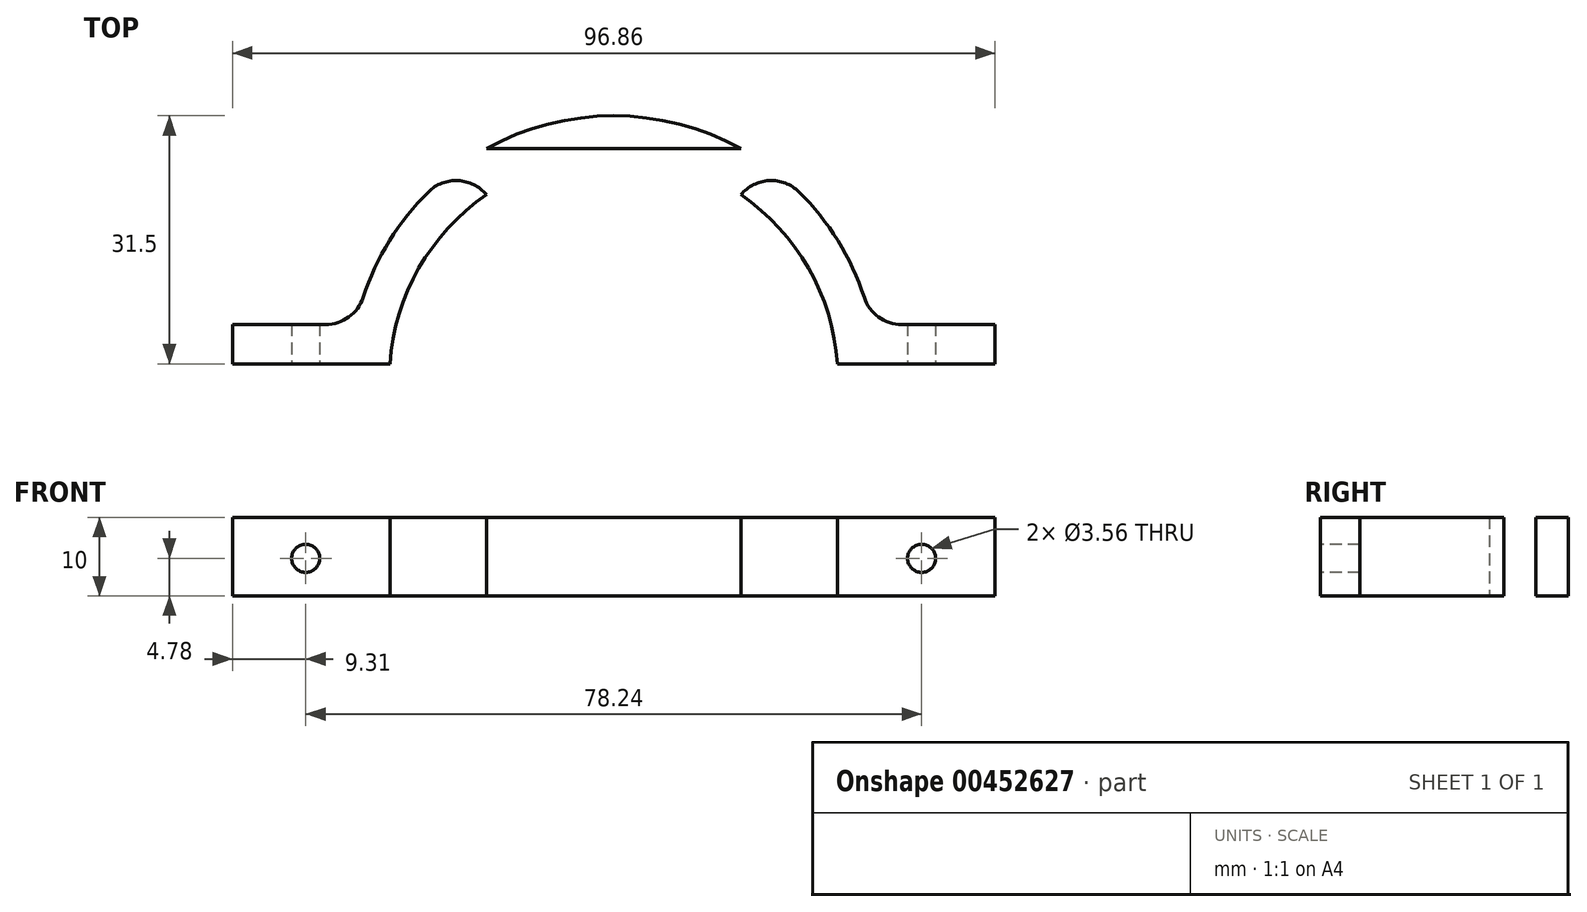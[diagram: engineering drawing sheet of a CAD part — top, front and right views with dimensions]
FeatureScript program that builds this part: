
annotation { "Feature Type Name" : "Feature", "Feature Type Description" : "" }
export const myFeature = defineFeature(function(context is Context, id is Id, definition is map)
    precondition{}
    {
        {
            var Q0;
            Q0=qCreatedBy(makeId("Top.planeOp"),FACE);
            var sketch = newSketch(context, id + "F0", { "sketchPlane" : qUnion([Q0])});
            skCircle(sketch, "E0", {"center": v(0, 0) * mm, "radius": 28.5 * mm, "construction": true});
            skLineSegment(sketch, "E1", {"start": v(-71.53, 0) * mm, "end": v(71.36, 0) * mm, "construction": true});
            skLineSegment(sketch, "E2", {"start": v(-71.7, 2) * mm, "end": v(71.19, 2) * mm, "construction": true});
            skArc(sketch, "E3", {"start": v(28.43, 2) * mm, "mid": v(0, 28.5) * mm, "end": v(-28.43, 2) * mm});
            skArc(sketch, "E4", {"start": v(33.44, 2) * mm, "mid": v(0, 33.5) * mm, "end": v(-33.44, 2) * mm});
            skLineSegment(sketch, "E5", {"start": v(-33.44, 2) * mm, "end": v(-28.43, 2) * mm});
            skLineSegment(sketch, "E6", {"start": v(28.43, 2) * mm, "end": v(33.44, 2) * mm});
            skLineSegment(sketch, "E7.bottom", {"start": v(-28.43, 2) * mm, "end": v(-48.43, 2) * mm});
            skLineSegment(sketch, "E7.top", {"start": v(-28.43, 7) * mm, "end": v(-48.43, 7) * mm});
            skLineSegment(sketch, "E7.left", {"start": v(-28.43, 2) * mm, "end": v(-28.43, 7) * mm});
            skLineSegment(sketch, "E7.right", {"start": v(-48.43, 2) * mm, "end": v(-48.43, 7) * mm});
            skLineSegment(sketch, "E8.bottom", {"start": v(28.43, 2) * mm, "end": v(48.43, 2) * mm});
            skLineSegment(sketch, "E8.top", {"start": v(28.43, 7) * mm, "end": v(48.43, 7) * mm});
            skLineSegment(sketch, "E8.left", {"start": v(28.43, 2) * mm, "end": v(28.43, 7) * mm});
            skLineSegment(sketch, "E8.right", {"start": v(48.43, 2) * mm, "end": v(48.43, 7) * mm});
            skLineSegment(sketch, "E9.bottom", {"start": v(-16.17, 33.5) * mm, "end": v(16.17, 33.5) * mm});
            skLineSegment(sketch, "E9.top", {"start": v(-16.17, 29.34) * mm, "end": v(16.17, 29.34) * mm});
            skLineSegment(sketch, "E9.left", {"start": v(-16.17, 33.5) * mm, "end": v(-16.17, 29.34) * mm});
            skLineSegment(sketch, "E9.right", {"start": v(16.17, 33.5) * mm, "end": v(16.17, 29.34) * mm});
            skPoint(sketch, "E10", {"position": v(0, 33.5) * mm});
            skLineSegment(sketch, "E11.top", {"start": v(-16.17, 23.47) * mm, "end": v(16.17, 23.47) * mm});
            skLineSegment(sketch, "E11.left", {"start": v(-16.17, 29.34) * mm, "end": v(-16.17, 23.47) * mm});
            skLineSegment(sketch, "E11.right", {"start": v(16.17, 29.34) * mm, "end": v(16.17, 23.47) * mm});
            skLineSegment(sketch, "E12.top", {"start": v(-16.17, 38.5) * mm, "end": v(16.17, 38.5) * mm});
            skLineSegment(sketch, "E12.left", {"start": v(-16.17, 33.5) * mm, "end": v(-16.17, 38.5) * mm});
            skLineSegment(sketch, "E12.right", {"start": v(16.17, 33.5) * mm, "end": v(16.17, 38.5) * mm});
            skSolve(sketch);
        }
        {
            var Q0;
            Q0=makeQuery(id+"F0.imprint","IMPRINT",FACE,{"disambiguationData":[TD([[makeQuery(id+"F0.imprint","IMPRINT",EDGE,{"derivedFrom":sQuery(id+"F0.wireOp",EDGE,"E3")}),-1.0]])]});
            var Q1;
            {var subQ5=sQuery(id+"F0.wireOp",EDGE,"E7.right");Q1=makeQuery(id+"F0.imprint","IMPRINT",FACE,{"disambiguationData":[TD([[makeQuery(id+"F0.imprint","IMPRINT",EDGE,{"derivedFrom":subQ5}),-1.0]])]});}
            var Q2;
            {var subQ5=sQuery(id+"F0.wireOp",EDGE,"E7.left");Q2=makeQuery(id+"F0.imprint","IMPRINT",FACE,{"disambiguationData":[TD([[makeQuery(id+"F0.imprint","IMPRINT",EDGE,{"derivedFrom":subQ5}),1.0]])]});}
            var Q3;
            {var subQ5=sQuery(id+"F0.wireOp",EDGE,"E8.left");Q3=makeQuery(id+"F0.imprint","IMPRINT",FACE,{"disambiguationData":[TD([[makeQuery(id+"F0.imprint","IMPRINT",EDGE,{"derivedFrom":subQ5}),-1.0]])]});}
            var Q4;
            {var subQ5=sQuery(id+"F0.wireOp",EDGE,"E8.right");Q4=makeQuery(id+"F0.imprint","IMPRINT",FACE,{"disambiguationData":[TD([[makeQuery(id+"F0.imprint","IMPRINT",EDGE,{"derivedFrom":subQ5}),1.0]])]});}
            var Q5;
            {var subQ0=sQuery(id+"F0.wireOp",EDGE,"E7.left");Q5=makeQuery(id+"F0.imprint","IMPRINT",FACE,{"disambiguationData":[TD([[makeQuery(id+"F0.imprint","IMPRINT",EDGE,{"derivedFrom":subQ0}),-1.0]])]});}
            var Q6;
            {var subQ0=sQuery(id+"F0.wireOp",EDGE,"E9.top");var subQ4=sQuery(id+"F0.wireOp",EDGE,"E3");var subQ7=makeQuery(id+"F0.imprint","INTERSECT",VERTEX,{"disambiguationData":[OD(0.0)],"derivedFrom":[subQ4,subQ0]});Q6=makeQuery(id+"F0.imprint","IMPRINT",FACE,{"disambiguationData":[TD([[makeQuery(id+"F0.imprint","IMPRINT",EDGE,{"disambiguationData":[TD([[subQ7,-1.0]])],"derivedFrom":subQ4}),-1.0]])]});}
            var Q7;
            {var subQ0=sQuery(id+"F0.wireOp",EDGE,"E8.left");Q7=makeQuery(id+"F0.imprint","IMPRINT",FACE,{"disambiguationData":[TD([[makeQuery(id+"F0.imprint","IMPRINT",EDGE,{"derivedFrom":subQ0}),1.0]])]});}
            var Q8;
            {var subQ0=sQuery(id+"F0.wireOp",EDGE,"E9.top");Q8=makeQuery(id+"F0.imprint","IMPRINT",FACE,{"disambiguationData":[TD([[makeQuery(id+"F0.imprint","IMPRINT",EDGE,{"derivedFrom":subQ0}),1.0]])]});}
            extrude(context, id + "F1", {"entities" : qUnion([Q0, Q1, Q2, Q3, Q4, Q5, Q6, Q7, Q8]), "depth" : 10 * mm});
        }
        {
            var Q0;
            Q0=makeQuery(id+"F1.opExtrude","SWEPT_FACE",FACE,{"disambiguationData":[OSD([sQuery(id+"F0.wireOp",EDGE,"E11.top")])]});
            var sketch = newSketch(context, id + "F2", { "sketchPlane" : qUnion([Q0])});
            skPoint(sketch, "E13", {"position": v(0, 5) * mm});
            skLineSegment(sketch, "E14", {"start": v(0, 0) * mm, "end": v(0, 10) * mm, "construction": true});
            skSolve(sketch);
        }
        {
            var Q0;
            Q0=sQuery(id+"F2.wireOp",VERTEX,"E13");
            var Q1;
            Q1=makeQuery(id+"F1.opExtrude","SWEPT_BODY",BODY,{"disambiguationData":[OSD([sQuery(id+"F0.wireOp",EDGE,"E3"),sQuery(id+"F0.wireOp",EDGE,"E4"),sQuery(id+"F0.wireOp",EDGE,"E7.bottom"),sQuery(id+"F0.wireOp",EDGE,"E7.top"),sQuery(id+"F0.wireOp",EDGE,"E7.right"),sQuery(id+"F0.wireOp",EDGE,"E8.bottom"),sQuery(id+"F0.wireOp",EDGE,"E8.top"),sQuery(id+"F0.wireOp",EDGE,"E8.right"),sQuery(id+"F0.wireOp",EDGE,"E9.bottom"),sQuery(id+"F0.wireOp",EDGE,"E9.left"),sQuery(id+"F0.wireOp",EDGE,"E9.right"),sQuery(id+"F0.wireOp",EDGE,"E9.top"),sQuery(id+"F0.wireOp",EDGE,"E11.top")])]});
            hole(context, id + "F3", {"style" : HoleStyle.C_BORE, "endStyle" : HoleEndStyle.THROUGH, "holeDiameter" : 3.56 * mm, "cBoreDiameter" : 7.62 * mm, "cBoreDepth" : 10 * mm, "isTappedThrough" : true, "tappedDepth" : 12 * mm, "tapClearance" : 3, "locations" : qUnion([Q0]), "scope" : qUnion([Q1])});
        }
        {
            var Q0;
            {var subQ0=sQuery(id+"F0.wireOp",EDGE,"E11.top");Q0=makeQuery(id+"F0.imprint","IMPRINT",FACE,{"disambiguationData":[TD([[makeQuery(id+"F0.imprint","IMPRINT",EDGE,{"derivedFrom":subQ0}),1.0]])]});}
            extrude(context, id + "F4", {"entities" : qUnion([Q0]), "operationType" : NewBodyOperationType.REMOVE, "endBound" : BoundingType.THROUGH_ALL, "depth" : 25 * mm});
        }
        {
            var Q0;
            Q0=makeQuery(id+"F1.opExtrude","SWEPT_FACE",FACE,{"disambiguationData":[OSD([sQuery(id+"F0.wireOp",EDGE,"E7.bottom")])]});
            var sketch = newSketch(context, id + "F5", { "sketchPlane" : qUnion([Q0])});
            skPoint(sketch, "E15", {"position": v(-39.12, 4.78) * mm});
            skPoint(sketch, "E16.MirrorP", {"position": v(39.12, 4.78) * mm});
            skSolve(sketch);
        }
        {
            var Q0;
            Q0=sQuery(id+"F5.wireOp",VERTEX,"E15");
            var Q1;
            Q1=sQuery(id+"F5.wireOp",VERTEX,"E16.MirrorP");
            var Q2;
            Q2=makeQuery(id+"F1.opExtrude","SWEPT_BODY",BODY,{"disambiguationData":[OSD([sQuery(id+"F0.wireOp",EDGE,"E3"),sQuery(id+"F0.wireOp",EDGE,"E4"),sQuery(id+"F0.wireOp",EDGE,"E7.bottom"),sQuery(id+"F0.wireOp",EDGE,"E7.top"),sQuery(id+"F0.wireOp",EDGE,"E7.right"),sQuery(id+"F0.wireOp",EDGE,"E8.bottom"),sQuery(id+"F0.wireOp",EDGE,"E8.top"),sQuery(id+"F0.wireOp",EDGE,"E8.right"),sQuery(id+"F0.wireOp",EDGE,"E9.left"),sQuery(id+"F0.wireOp",EDGE,"E9.right"),sQuery(id+"F0.wireOp",EDGE,"E9.top"),sQuery(id+"F0.wireOp",EDGE,"E11.top"),sQuery(id+"F0.wireOp",EDGE,"E12.top"),sQuery(id+"F0.wireOp",EDGE,"E12.left"),sQuery(id+"F0.wireOp",EDGE,"E12.right")])]});
            hole(context, id + "F6", {"style" : HoleStyle.SIMPLE, "endStyle" : HoleEndStyle.THROUGH, "holeDiameter" : 3.56 * mm, "isTappedThrough" : true, "tappedDepth" : 12 * mm, "tapClearance" : 3, "locations" : qUnion([Q0, Q1]), "scope" : qUnion([Q2])});
        }
        {
            var Q0;
            Q0=makeQuery(id+"F1.opExtrude","SWEPT_EDGE",EDGE,{"disambiguationData":[OSD([sQuery(id+"F0.wireOp",EDGE,"E4"),sQuery(id+"F0.wireOp",EDGE,"E7.top")])]});
            var Q1;
            Q1=makeQuery(id+"F1.opExtrude","SWEPT_EDGE",EDGE,{"disambiguationData":[OSD([sQuery(id+"F0.wireOp",EDGE,"E4"),sQuery(id+"F0.wireOp",EDGE,"E8.top")])]});
            var Q2;
            Q2=makeQuery(id+"F1.opExtrude","SWEPT_EDGE",EDGE,{"disambiguationData":[OSD([sQuery(id+"F0.wireOp",EDGE,"E4"),sQuery(id+"F0.wireOp",EDGE,"E9.right"),sQuery(id+"F0.wireOp",EDGE,"E9.top"),sQuery(id+"F0.wireOp",EDGE,"E11.right")])]});
            var Q3;
            Q3=makeQuery(id+"F1.opExtrude","SWEPT_EDGE",EDGE,{"disambiguationData":[OSD([sQuery(id+"F0.wireOp",EDGE,"E4"),sQuery(id+"F0.wireOp",EDGE,"E9.left"),sQuery(id+"F0.wireOp",EDGE,"E9.top"),sQuery(id+"F0.wireOp",EDGE,"E11.left")])]});
            fillet(context, id + "F7", {"entities" : qUnion([Q0, Q1, Q2, Q3]), "radius" : 5 * mm, "tangentPropagation" : true, "allowEdgeOverflow" : false});
        }
    });
